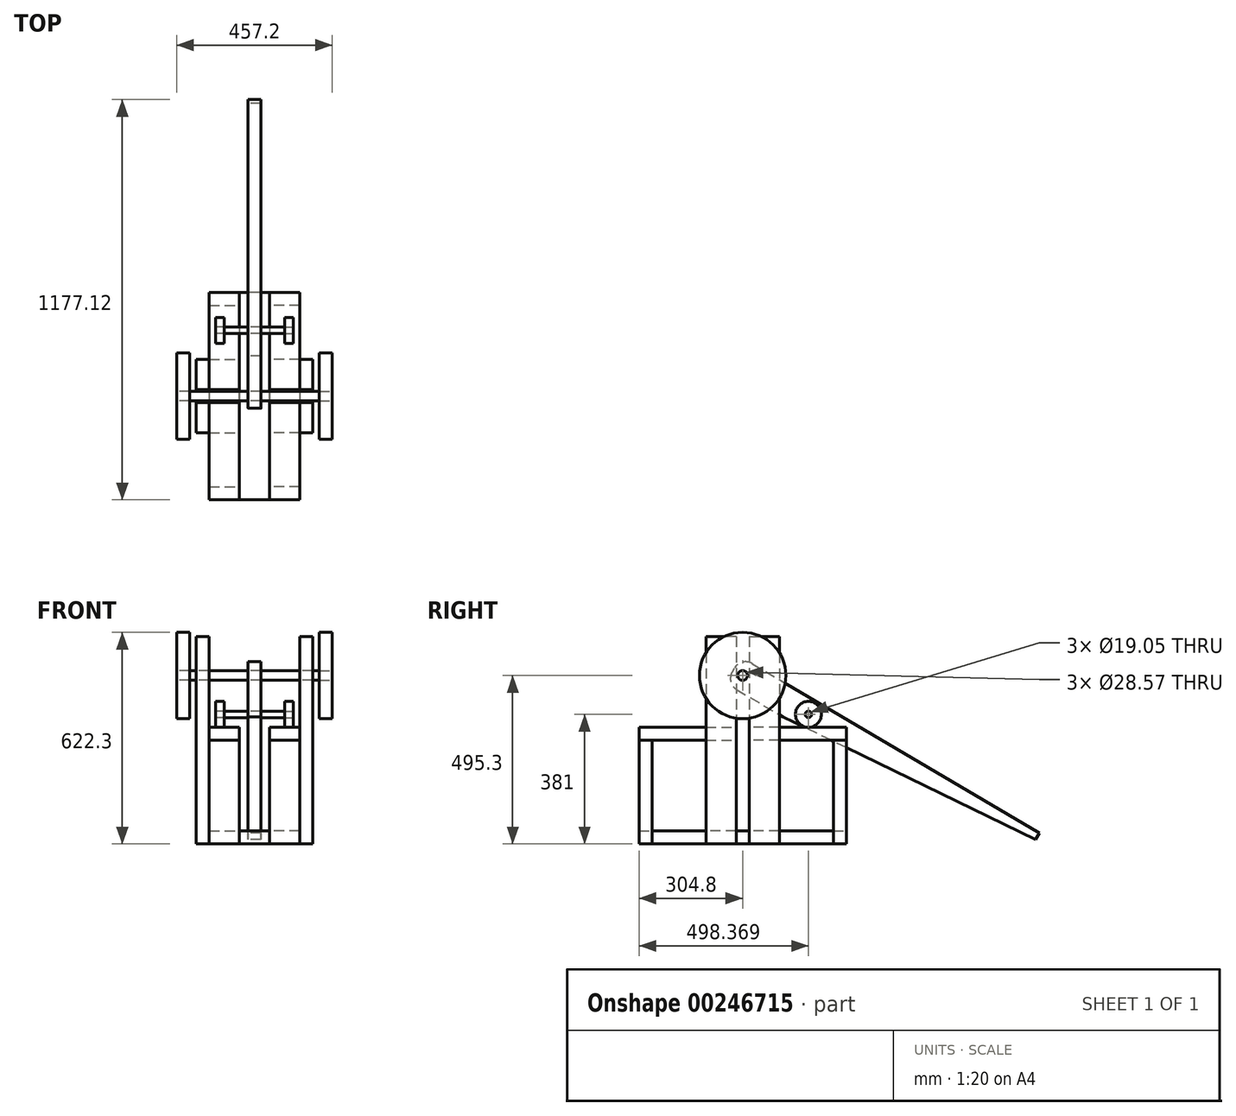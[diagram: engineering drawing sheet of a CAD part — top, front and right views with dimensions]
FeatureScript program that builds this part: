
annotation { "Feature Type Name" : "Feature", "Feature Type Description" : "" }
export const myFeature = defineFeature(function(context is Context, id is Id, definition is map)
    precondition{}
    {
        {
            var Q0;
            Q0=qCreatedBy(makeId("Right.planeOp"),FACE);
            var sketch = newSketch(context, id + "F0", { "sketchPlane" : qUnion([Q0])});
            skLineSegment(sketch, "E0.bottom", {"start": v(-304.8, 0) * mm, "end": v(304.8, 0) * mm});
            skLineSegment(sketch, "E0.top", {"start": v(-304.8, 38.1) * mm, "end": v(304.8, 38.1) * mm});
            skLineSegment(sketch, "E0.left", {"start": v(-304.8, 0) * mm, "end": v(-304.8, 38.1) * mm});
            skLineSegment(sketch, "E0.right", {"start": v(304.8, 0) * mm, "end": v(304.8, 38.1) * mm});
            skPoint(sketch, "E0.middle", {"position": v(0, 19.05) * mm});
            skSolve(sketch);
        }
        {
            var Q0;
            Q0=makeQuery(id+"F0.imprint","IMPRINT",FACE,{"disambiguationData":[TD([[makeQuery(id+"F0.imprint","IMPRINT",EDGE,{"derivedFrom":sQuery(id+"F0.wireOp",EDGE,"E0.bottom")}),1.0]])]});
            extrude(context, id + "F1", {"entities" : qUnion([Q0]), "endBound" : BoundingType.SYMMETRIC, "depth" : 88.9 * mm});
        }
        {
            var Q0;
            Q0=makeQuery(id+"F1.opExtrude","CAP_FACE",FACE,{"disambiguationData":[OSD([sQuery(id+"F0.wireOp",EDGE,"E0.bottom"),sQuery(id+"F0.wireOp",EDGE,"E0.top"),sQuery(id+"F0.wireOp",EDGE,"E0.left"),sQuery(id+"F0.wireOp",EDGE,"E0.right")])],"isStart":false});
            var sketch = newSketch(context, id + "F2", { "sketchPlane" : qUnion([Q0])});
            skLineSegment(sketch, "E1.bottom", {"start": v(-304.8, 0) * mm, "end": v(-266.7, 0) * mm});
            skLineSegment(sketch, "E1.top", {"start": v(-304.8, 304.8) * mm, "end": v(-266.7, 304.8) * mm});
            skLineSegment(sketch, "E1.left", {"start": v(-304.8, 0) * mm, "end": v(-304.8, 304.8) * mm});
            skLineSegment(sketch, "E1.right", {"start": v(-266.7, 0) * mm, "end": v(-266.7, 304.8) * mm});
            skSolve(sketch);
        }
        {
            var Q0;
            {var subQ0=sQuery(id+"F2.wireOp",EDGE,"E1.top");Q0=makeQuery(id+"F2.imprint","IMPRINT",FACE,{"disambiguationData":[TD([[makeQuery(id+"F2.imprint","IMPRINT",EDGE,{"derivedFrom":subQ0}),-1.0]])]});}
            var Q1;
            {var subQ0=sQuery(id+"F2.wireOp",EDGE,"E1.bottom");Q1=makeQuery(id+"F2.imprint","IMPRINT",FACE,{"disambiguationData":[TD([[makeQuery(id+"F2.imprint","IMPRINT",EDGE,{"derivedFrom":subQ0}),1.0]])]});}
            extrude(context, id + "F3", {"entities" : qUnion([Q0, Q1]), "depth" : 88.9 * mm});
        }
        {
            var Q0;
            Q0=makeQuery(id+"F3.opExtrude","SWEPT_BODY",BODY,{"disambiguationData":[OSD([sQuery(id+"F2.wireOp",EDGE,"E1.bottom"),sQuery(id+"F2.wireOp",EDGE,"E1.top"),sQuery(id+"F2.wireOp",EDGE,"E1.left"),sQuery(id+"F2.wireOp",EDGE,"E1.right")])]});
            var Q1;
            Q1=qCreatedBy(makeId("Right.planeOp"),FACE);
            mirror(context, id + "F4", {"entities" : qUnion([Q0]), "mirrorPlane" : qUnion([Q1])});
        }
        {
            var Q0;
            Q0=makeQuery(id+"F1.opExtrude","CAP_FACE",FACE,{"disambiguationData":[OSD([sQuery(id+"F0.wireOp",EDGE,"E0.bottom"),sQuery(id+"F0.wireOp",EDGE,"E0.top"),sQuery(id+"F0.wireOp",EDGE,"E0.left"),sQuery(id+"F0.wireOp",EDGE,"E0.right")])],"isStart":false});
            var sketch = newSketch(context, id + "F5", { "sketchPlane" : qUnion([Q0])});
            skLineSegment(sketch, "E2.bottom", {"start": v(-304.8, 342.9) * mm, "end": v(-19.05, 342.9) * mm});
            skLineSegment(sketch, "E2.top", {"start": v(-304.8, 304.8) * mm, "end": v(-19.05, 304.8) * mm});
            skLineSegment(sketch, "E2.left", {"start": v(-304.8, 342.9) * mm, "end": v(-304.8, 304.8) * mm});
            skLineSegment(sketch, "E2.right", {"start": v(-19.05, 342.9) * mm, "end": v(-19.05, 304.8) * mm});
            skSolve(sketch);
        }
        {
            var Q0;
            Q0=makeQuery(id+"F5.imprint","IMPRINT",FACE,{"disambiguationData":[TD([[makeQuery(id+"F5.imprint","IMPRINT",EDGE,{"derivedFrom":sQuery(id+"F5.wireOp",EDGE,"E2.bottom")}),-1.0]])]});
            extrude(context, id + "F6", {"entities" : qUnion([Q0]), "depth" : 88.9 * mm});
        }
        {
            var Q0;
            Q0=makeQuery(id+"F6.opExtrude","SWEPT_BODY",BODY,{"disambiguationData":[OSD([sQuery(id+"F5.wireOp",EDGE,"E2.bottom"),sQuery(id+"F5.wireOp",EDGE,"E2.top"),sQuery(id+"F5.wireOp",EDGE,"E2.left"),sQuery(id+"F5.wireOp",EDGE,"E2.right")])]});
            var Q1;
            Q1=qCreatedBy(makeId("Right.planeOp"),FACE);
            mirror(context, id + "F7", {"entities" : qUnion([Q0]), "mirrorPlane" : qUnion([Q1])});
        }
        {
            var Q0;
            Q0=makeQuery(id+"F3.opExtrude","SWEPT_BODY",BODY,{"disambiguationData":[OSD([sQuery(id+"F2.wireOp",EDGE,"E1.bottom"),sQuery(id+"F2.wireOp",EDGE,"E1.top"),sQuery(id+"F2.wireOp",EDGE,"E1.left"),sQuery(id+"F2.wireOp",EDGE,"E1.right")])]});
            var Q1;
            Q1=makeQuery(id+"F6.opExtrude","SWEPT_BODY",BODY,{"disambiguationData":[OSD([sQuery(id+"F5.wireOp",EDGE,"E2.bottom"),sQuery(id+"F5.wireOp",EDGE,"E2.top"),sQuery(id+"F5.wireOp",EDGE,"E2.left"),sQuery(id+"F5.wireOp",EDGE,"E2.right")])]});
            var Q2;
            Q2=makeQuery(id+"F7.opPattern","COPY",BODY,{"derivedFrom":makeQuery(id+"F6.opExtrude","SWEPT_BODY",BODY,{"disambiguationData":[OSD([sQuery(id+"F5.wireOp",EDGE,"E2.bottom"),sQuery(id+"F5.wireOp",EDGE,"E2.top"),sQuery(id+"F5.wireOp",EDGE,"E2.left"),sQuery(id+"F5.wireOp",EDGE,"E2.right")])]}),"instanceName":"1"});
            var Q3;
            Q3=makeQuery(id+"F4.opPattern","COPY",BODY,{"derivedFrom":makeQuery(id+"F3.opExtrude","SWEPT_BODY",BODY,{"disambiguationData":[OSD([sQuery(id+"F2.wireOp",EDGE,"E1.bottom"),sQuery(id+"F2.wireOp",EDGE,"E1.top"),sQuery(id+"F2.wireOp",EDGE,"E1.left"),sQuery(id+"F2.wireOp",EDGE,"E1.right")])]}),"instanceName":"1"});
            var Q4;
            Q4=qCreatedBy(makeId("Front.planeOp"),FACE);
            mirror(context, id + "F8", {"entities" : qUnion([Q0, Q1, Q2, Q3]), "mirrorPlane" : qUnion([Q4])});
        }
        {
            var Q0;
            Q0=makeQuery(id+"F6.opExtrude","CAP_FACE",FACE,{"disambiguationData":[OSD([sQuery(id+"F5.wireOp",EDGE,"E2.bottom"),sQuery(id+"F5.wireOp",EDGE,"E2.top"),sQuery(id+"F5.wireOp",EDGE,"E2.left"),sQuery(id+"F5.wireOp",EDGE,"E2.right")])],"isStart":false});
            var sketch = newSketch(context, id + "F9", { "sketchPlane" : qUnion([Q0])});
            skLineSegment(sketch, "E3.bottom", {"start": v(-19.05, 609.6) * mm, "end": v(-107.95, 609.6) * mm});
            skLineSegment(sketch, "E3.top", {"start": v(-19.05, 0) * mm, "end": v(-107.95, 0) * mm});
            skLineSegment(sketch, "E3.left", {"start": v(-19.05, 609.6) * mm, "end": v(-19.05, 0) * mm});
            skLineSegment(sketch, "E3.right", {"start": v(-107.95, 609.6) * mm, "end": v(-107.95, 0) * mm});
            skSolve(sketch);
        }
        {
            var Q0;
            {var subQ0=sQuery(id+"F9.wireOp",EDGE,"E3.bottom");Q0=makeQuery(id+"F9.imprint","IMPRINT",FACE,{"disambiguationData":[TD([[makeQuery(id+"F9.imprint","IMPRINT",EDGE,{"derivedFrom":subQ0}),1.0]])]});}
            var Q1;
            {var subQ0=sQuery(id+"F9.wireOp",EDGE,"E3.left");var subQ1=makeQuery(id+"F6.opExtrude","CAP_EDGE",EDGE,{"disambiguationData":[OSD([sQuery(id+"F5.wireOp",EDGE,"E2.bottom")])],"isStart":false});var subQ2=makeQuery(id+"F9.imprint","INTERSECT",VERTEX,{"derivedFrom":[subQ1,subQ0]});Q1=makeQuery(id+"F9.imprint","IMPRINT",FACE,{"disambiguationData":[TD([[makeQuery(id+"F9.imprint","IMPRINT",EDGE,{"disambiguationData":[TD([[subQ2,-1.0]])],"derivedFrom":subQ0}),-1.0]])]});}
            var Q2;
            {var subQ0=sQuery(id+"F9.wireOp",EDGE,"E3.top");Q2=makeQuery(id+"F9.imprint","IMPRINT",FACE,{"disambiguationData":[TD([[makeQuery(id+"F9.imprint","IMPRINT",EDGE,{"derivedFrom":subQ0}),-1.0]])]});}
            extrude(context, id + "F10", {"entities" : qUnion([Q0, Q1, Q2]), "depth" : 38.1 * mm});
        }
        {
            var Q0;
            Q0=makeQuery(id+"F10.opExtrude","SWEPT_BODY",BODY,{"disambiguationData":[OSD([sQuery(id+"F9.wireOp",EDGE,"E3.bottom"),sQuery(id+"F9.wireOp",EDGE,"E3.top"),sQuery(id+"F9.wireOp",EDGE,"E3.left"),sQuery(id+"F9.wireOp",EDGE,"E3.right")])]});
            var Q1;
            Q1=qCreatedBy(makeId("Right.planeOp"),FACE);
            mirror(context, id + "F11", {"entities" : qUnion([Q0]), "mirrorPlane" : qUnion([Q1])});
        }
        {
            var Q0;
            Q0=makeQuery(id+"F10.opExtrude","SWEPT_BODY",BODY,{"disambiguationData":[OSD([sQuery(id+"F9.wireOp",EDGE,"E3.bottom"),sQuery(id+"F9.wireOp",EDGE,"E3.top"),sQuery(id+"F9.wireOp",EDGE,"E3.left"),sQuery(id+"F9.wireOp",EDGE,"E3.right")])]});
            var Q1;
            Q1=makeQuery(id+"F11.opPattern","COPY",BODY,{"derivedFrom":makeQuery(id+"F10.opExtrude","SWEPT_BODY",BODY,{"disambiguationData":[OSD([sQuery(id+"F9.wireOp",EDGE,"E3.bottom"),sQuery(id+"F9.wireOp",EDGE,"E3.top"),sQuery(id+"F9.wireOp",EDGE,"E3.left"),sQuery(id+"F9.wireOp",EDGE,"E3.right")])]}),"instanceName":"1"});
            var Q2;
            Q2=qCreatedBy(makeId("Front.planeOp"),FACE);
            mirror(context, id + "F12", {"entities" : qUnion([Q0, Q1]), "mirrorPlane" : qUnion([Q2])});
        }
        {
            var Q0;
            Q0=qCreatedBy(makeId("Top.planeOp"),FACE);
            var sketch = newSketch(context, id + "F13", { "sketchPlane" : qUnion([Q0])});
            skLineSegment(sketch, "E4.bottom", {"start": v(-133.35, 107.95) * mm, "end": v(-44.45, 107.95) * mm});
            skLineSegment(sketch, "E4.top", {"start": v(-133.35, -107.95) * mm, "end": v(-44.45, -107.95) * mm});
            skLineSegment(sketch, "E4.left", {"start": v(-133.35, 107.95) * mm, "end": v(-133.35, -107.95) * mm});
            skLineSegment(sketch, "E4.right", {"start": v(-44.45, 107.95) * mm, "end": v(-44.45, -107.95) * mm});
            skSolve(sketch);
        }
        {
            var Q0;
            Q0=makeQuery(id+"F13.imprint","IMPRINT",FACE,{"disambiguationData":[TD([[makeQuery(id+"F13.imprint","IMPRINT",EDGE,{"derivedFrom":sQuery(id+"F13.wireOp",EDGE,"E4.bottom")}),-1.0]])]});
            extrude(context, id + "F14", {"entities" : qUnion([Q0]), "depth" : 38.1 * mm});
        }
        {
            var Q0;
            Q0=makeQuery(id+"F14.opExtrude","SWEPT_BODY",BODY,{"disambiguationData":[OSD([sQuery(id+"F13.wireOp",EDGE,"E4.bottom"),sQuery(id+"F13.wireOp",EDGE,"E4.top"),sQuery(id+"F13.wireOp",EDGE,"E4.left"),sQuery(id+"F13.wireOp",EDGE,"E4.right")])]});
            var Q1;
            Q1=qCreatedBy(makeId("Right.planeOp"),FACE);
            mirror(context, id + "F15", {"entities" : qUnion([Q0]), "mirrorPlane" : qUnion([Q1])});
        }
        {
            var Q0;
            Q0=qCreatedBy(makeId("Right.planeOp"),FACE);
            var sketch = newSketch(context, id + "F16", { "sketchPlane" : qUnion([Q0])});
            skCircle(sketch, "E5", {"center": v(0, 495.3) * mm, "radius": 14.29 * mm});
            skSolve(sketch);
        }
        {
            var Q0;
            Q0 = qSketchRegion(id + "F16", true);
            extrude(context, id + "F17", {"entities" : qUnion([Q0]), "endBound" : BoundingType.SYMMETRIC, "depth" : 457.2 * mm});
        }
        {
            var Q0;
            Q0=makeQuery(id+"F17.opExtrude","CAP_FACE",FACE,{"disambiguationData":[OSD([sQuery(id+"F16.wireOp",EDGE,"E5")])],"isStart":false});
            var sketch = newSketch(context, id + "F18", { "sketchPlane" : qUnion([Q0])});
            skCircle(sketch, "E6", {"center": v(0, 495.3) * mm, "radius": 14.29 * mm});
            skCircle(sketch, "E7", {"center": v(0, 495.3) * mm, "radius": 127 * mm});
            skSolve(sketch);
        }
        {
            var Q0;
            Q0=makeQuery(id+"F18.imprint","IMPRINT",FACE,{"disambiguationData":[TD([[makeQuery(id+"F18.imprint","IMPRINT",EDGE,{"derivedFrom":sQuery(id+"F18.wireOp",EDGE,"E6")}),-1.0]])]});
            extrude(context, id + "F19", {"entities" : qUnion([Q0]), "oppositeDirection" : true, "depth" : 38.1 * mm});
        }
        {
            var Q0;
            Q0=makeQuery(id+"F19.opExtrude","SWEPT_BODY",BODY,{"disambiguationData":[OSD([sQuery(id+"F18.wireOp",EDGE,"E6"),sQuery(id+"F18.wireOp",EDGE,"E7")])]});
            var Q1;
            Q1=qCreatedBy(makeId("Right.planeOp"),FACE);
            mirror(context, id + "F20", {"entities" : qUnion([Q0]), "mirrorPlane" : qUnion([Q1])});
        }
        {
            var Q0;
            Q0=qCreatedBy(makeId("Right.planeOp"),FACE);
            var sketch = newSketch(context, id + "F21", { "sketchPlane" : qUnion([Q0])});
            skCircle(sketch, "E8", {"center": v(193.57, 381) * mm, "radius": 38.1 * mm, "construction": true});
            skCircle(sketch, "E9", {"center": v(193.57, 381) * mm, "radius": 9.53 * mm});
            skSolve(sketch);
        }
        {
            var Q0;
            Q0=makeQuery(id+"F21.imprint","IMPRINT",FACE,{"disambiguationData":[TD([[makeQuery(id+"F21.imprint","IMPRINT",EDGE,{"derivedFrom":sQuery(id+"F21.wireOp",EDGE,"E9")}),1.0]])]});
            extrude(context, id + "F22", {"entities" : qUnion([Q0]), "endBound" : BoundingType.SYMMETRIC, "depth" : 228.6 * mm});
        }
        {
            var Q0;
            Q0=makeQuery(id+"F22.opExtrude","CAP_FACE",FACE,{"disambiguationData":[OSD([sQuery(id+"F21.wireOp",EDGE,"E9")])],"isStart":false});
            var sketch = newSketch(context, id + "F23", { "sketchPlane" : qUnion([Q0])});
            skCircle(sketch, "E10", {"center": v(193.57, 381) * mm, "radius": 38.1 * mm});
            skCircle(sketch, "E11", {"center": v(193.57, 381) * mm, "radius": 9.53 * mm});
            skSolve(sketch);
        }
        {
            var Q0;
            Q0=makeQuery(id+"F23.imprint","IMPRINT",FACE,{"disambiguationData":[TD([[makeQuery(id+"F23.imprint","IMPRINT",EDGE,{"derivedFrom":sQuery(id+"F23.wireOp",EDGE,"E10")}),1.0]])]});
            extrude(context, id + "F24", {"entities" : qUnion([Q0]), "oppositeDirection" : true, "depth" : 25.4 * mm});
        }
        {
            var Q0;
            Q0=makeQuery(id+"F24.opExtrude","SWEPT_BODY",BODY,{"disambiguationData":[OSD([sQuery(id+"F23.wireOp",EDGE,"E10"),sQuery(id+"F23.wireOp",EDGE,"E11")])]});
            var Q1;
            Q1=qCreatedBy(makeId("Right.planeOp"),FACE);
            mirror(context, id + "F25", {"entities" : qUnion([Q0]), "mirrorPlane" : qUnion([Q1])});
        }
        {
            var Q0;
            Q0=qCreatedBy(makeId("Right.planeOp"),FACE);
            var sketch = newSketch(context, id + "F26", { "sketchPlane" : qUnion([Q0])});
            skLineSegment(sketch, "E12", {"start": v(193.57, 381) * mm, "end": v(0, 495.3) * mm, "construction": true});
            skLineSegment(sketch, "E13", {"start": v(-27.34, 511.44) * mm, "end": v(-24.11, 516.91) * mm});
            skLineSegment(sketch, "E14", {"start": v(28.07, 530.35) * mm, "end": v(872.32, 31.83) * mm});
            skLineSegment(sketch, "E15", {"start": v(872.32, 31.83) * mm, "end": v(861.02, 12.7) * mm});
            skLineSegment(sketch, "E16.MirrorCS", {"start": v(-17.13, 453.8) * mm, "end": v(118.17, 373.9) * mm});
            skLineSegment(sketch, "E17.MirrorCS", {"start": v(-27.34, 511.44) * mm, "end": v(-30.57, 505.98) * mm});
            skLineSegment(sketch, "E18", {"start": v(861.02, 12.7) * mm, "end": v(118.17, 373.9) * mm});
            skPoint(sketch, "E19.orphan", {"position": v(827.12, -44.72) * mm});
            skPoint(sketch, "E20.MirrorCS.end.orphan", {"position": v(849.72, -6.45) * mm});
            skLineSegment(sketch, "E21", {"start": v(0, 0) * mm, "end": v(855.78, 0) * mm, "construction": true});
            skLineSegment(sketch, "E22", {"start": v(193.57, 381) * mm, "end": v(193.57, 29.21) * mm, "construction": true});
            skPoint(sketch, "E23.visualSharp", {"position": v(-4.74, 549.72) * mm});
            skArc(sketch, "E23.filletArc", {"start": v(28.07, 530.35) * mm, "mid": v(-0.8, 534.44) * mm, "end": v(-24.11, 516.91) * mm});
            skPoint(sketch, "E24.visualSharp", {"position": v(-49.94, 473.17) * mm});
            skArc(sketch, "E24.filletArc", {"start": v(-30.57, 505.98) * mm, "mid": v(-34.66, 477.1) * mm, "end": v(-17.13, 453.8) * mm});
            skCircle(sketch, "E25", {"center": v(0, 495.3) * mm, "radius": 14.29 * mm});
            skCircle(sketch, "E26", {"center": v(193.57, 381) * mm, "radius": 9.53 * mm});
            skSolve(sketch);
        }
        {
            var Q0;
            Q0=makeQuery(id+"F26.imprint","IMPRINT",FACE,{"disambiguationData":[TD([[makeQuery(id+"F26.imprint","IMPRINT",EDGE,{"derivedFrom":sQuery(id+"F26.wireOp",EDGE,"E13")}),-1.0]])]});
            extrude(context, id + "F27", {"entities" : qUnion([Q0]), "endBound" : BoundingType.SYMMETRIC, "depth" : 38.1 * mm});
        }
    });
